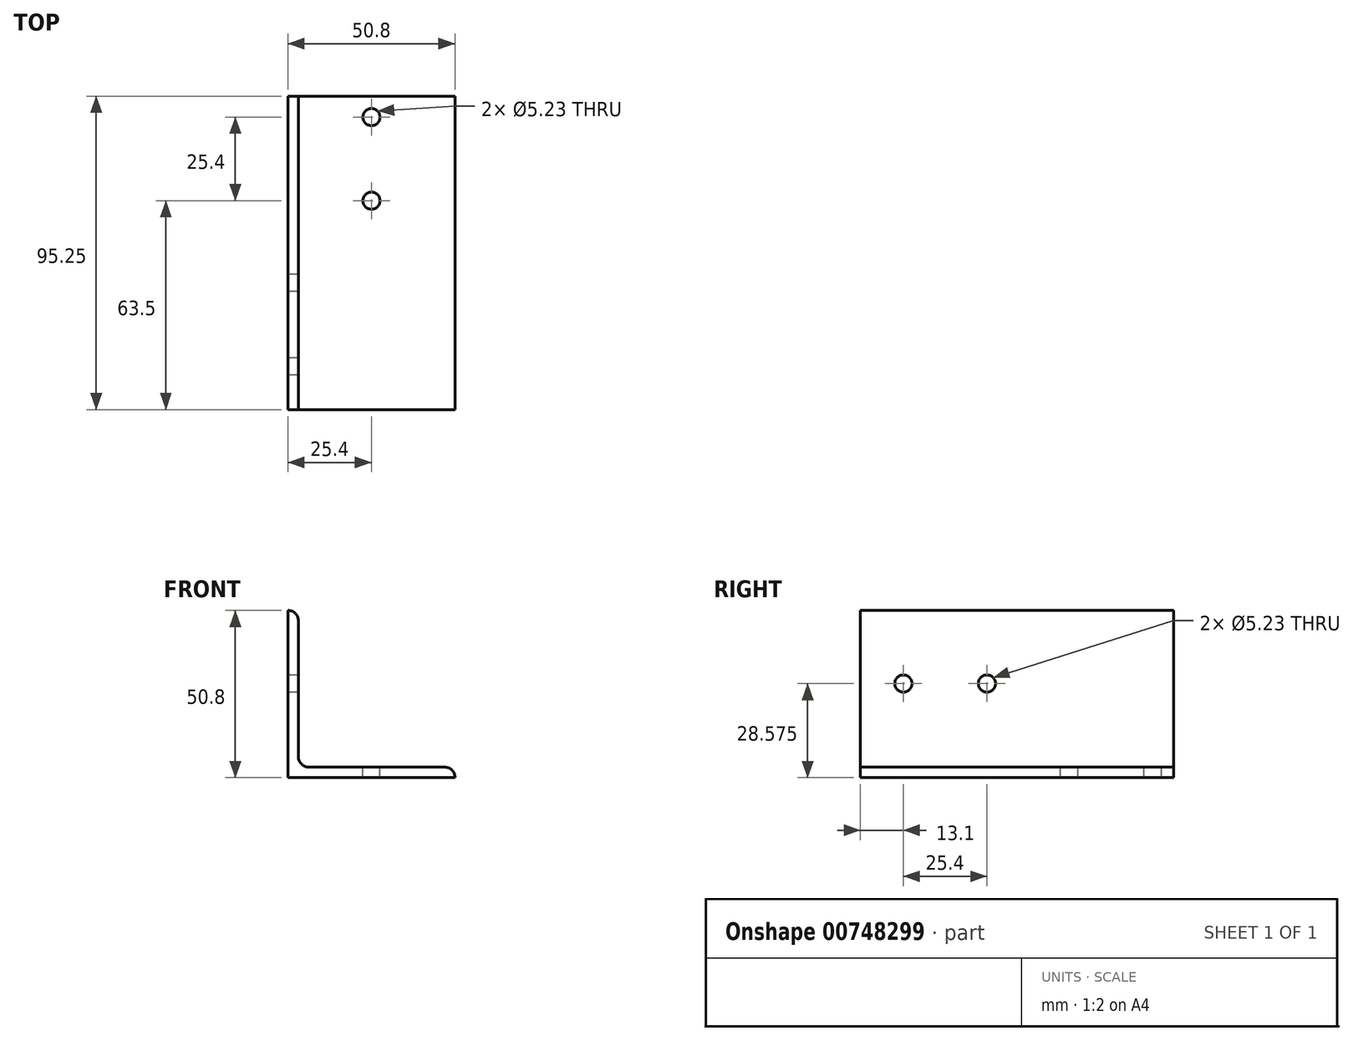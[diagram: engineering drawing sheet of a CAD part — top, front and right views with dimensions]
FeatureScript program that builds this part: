
annotation { "Feature Type Name" : "Feature", "Feature Type Description" : "" }
export const myFeature = defineFeature(function(context is Context, id is Id, definition is map)
    precondition{}
    {
        {
            var Q0;
            Q0=qCreatedBy(makeId("Front.planeOp"),FACE);
            var sketch = newSketch(context, id + "F0", { "sketchPlane" : qUnion([Q0])});
            skLineSegment(sketch, "E0", {"start": v(0, 0) * mm, "end": v(-50.8, 0) * mm});
            skLineSegment(sketch, "E1", {"start": v(-50.8, 0) * mm, "end": v(-50.8, 50.8) * mm});
            skLineSegment(sketch, "E2", {"start": v(-50.8, 50.8) * mm, "end": v(-50.8, 50.8) * mm});
            skLineSegment(sketch, "E3", {"start": v(-47.63, 47.63) * mm, "end": v(-47.63, 6.35) * mm});
            skLineSegment(sketch, "E4", {"start": v(-44.45, 3.18) * mm, "end": v(-3.18, 3.18) * mm});
            skLineSegment(sketch, "E5", {"start": v(0, 0) * mm, "end": v(0, 0) * mm});
            skPoint(sketch, "E6.visualSharp", {"position": v(-47.63, 3.18) * mm});
            skArc(sketch, "E6.filletArc", {"start": v(-47.63, 6.35) * mm, "mid": v(-46.7, 4.1) * mm, "end": v(-44.45, 3.18) * mm});
            skPoint(sketch, "E7.visualSharp", {"position": v(-47.63, 50.8) * mm});
            skArc(sketch, "E7.filletArc", {"start": v(-47.63, 47.63) * mm, "mid": v(-48.55, 49.87) * mm, "end": v(-50.8, 50.8) * mm});
            skPoint(sketch, "E8.visualSharp", {"position": v(0, 3.18) * mm});
            skArc(sketch, "E8.filletArc", {"start": v(0, 0) * mm, "mid": v(-0.93, 2.25) * mm, "end": v(-3.18, 3.18) * mm});
            skSolve(sketch);
        }
        {
            var Q0;
            Q0=qSketchRegion(id+"F0",true);
            extrude(context, id + "F1", {"entities" : qUnion([Q0]), "depth" : 95.25 * mm, "offsetDistance" : 25.4 * mm});
        }
        {
            var Q0;
            Q0=makeQuery(id+"F1.opExtrude","SWEPT_FACE",FACE,{"disambiguationData":[OSD([sQuery(id+"F0.wireOp",EDGE,"E4")])]});
            var sketch = newSketch(context, id + "F2", { "sketchPlane" : qUnion([Q0])});
            skLineSegment(sketch, "E9", {"start": v(-3.18, -6.35) * mm, "end": v(-44.45, -6.35) * mm, "construction": true});
            skCircle(sketch, "E10", {"center": v(-25.4, -6.35) * mm, "radius": 2.62 * mm});
            skLineSegment(sketch, "E11", {"start": v(-44.45, -31.75) * mm, "end": v(-3.18, -31.75) * mm, "construction": true});
            skCircle(sketch, "E12", {"center": v(-25.4, -31.75) * mm, "radius": 2.62 * mm});
            skLineSegment(sketch, "E13", {"start": v(-44.45, -47.63) * mm, "end": v(-3.18, -47.63) * mm, "construction": true});
            skLineSegment(sketch, "E14", {"start": v(-25.4, 0) * mm, "end": v(-25.4, -95.25) * mm, "construction": true});
            skSolve(sketch);
        }
        {
            var Q0;
            Q0=qSketchRegion(id+"F2",true);
            extrude(context, id + "F3", {"entities" : qUnion([Q0]), "operationType" : NewBodyOperationType.REMOVE, "endBound" : BoundingType.THROUGH_ALL, "oppositeDirection" : true, "depth" : 25.4 * mm, "offsetDistance" : 25.4 * mm});
        }
        {
            var Q0;
            Q0=makeQuery(id+"F1.opExtrude","SWEPT_FACE",FACE,{"disambiguationData":[OSD([sQuery(id+"F0.wireOp",EDGE,"E1")])]});
            var sketch = newSketch(context, id + "F4", { "sketchPlane" : qUnion([Q0])});
            skLineSegment(sketch, "E15", {"start": v(47.62, 50.8) * mm, "end": v(47.63, 0) * mm, "construction": true});
            skLineSegment(sketch, "E16", {"start": v(75.8, 50.8) * mm, "end": v(75.8, 0) * mm, "construction": true});
            skLineSegment(sketch, "E17", {"start": v(50.8, 0) * mm, "end": v(50.8, 50.8) * mm, "construction": true});
            skLineSegment(sketch, "E18", {"start": v(56.75, 50.8) * mm, "end": v(56.75, 0) * mm, "construction": true});
            skLineSegment(sketch, "E19", {"start": v(82.15, 50.8) * mm, "end": v(82.15, 0) * mm, "construction": true});
            skCircle(sketch, "E20", {"center": v(56.75, 28.58) * mm, "radius": 2.62 * mm});
            skCircle(sketch, "E21", {"center": v(82.15, 28.58) * mm, "radius": 2.62 * mm});
            skLineSegment(sketch, "E22", {"start": v(95.25, 28.58) * mm, "end": v(0, 28.58) * mm, "construction": true});
            skSolve(sketch);
        }
        {
            var Q0;
            Q0=qSketchRegion(id+"F4",true);
            extrude(context, id + "F5", {"entities" : qUnion([Q0]), "operationType" : NewBodyOperationType.REMOVE, "endBound" : BoundingType.THROUGH_ALL, "oppositeDirection" : true, "depth" : 25.4 * mm, "offsetDistance" : 25.4 * mm});
        }
    });
